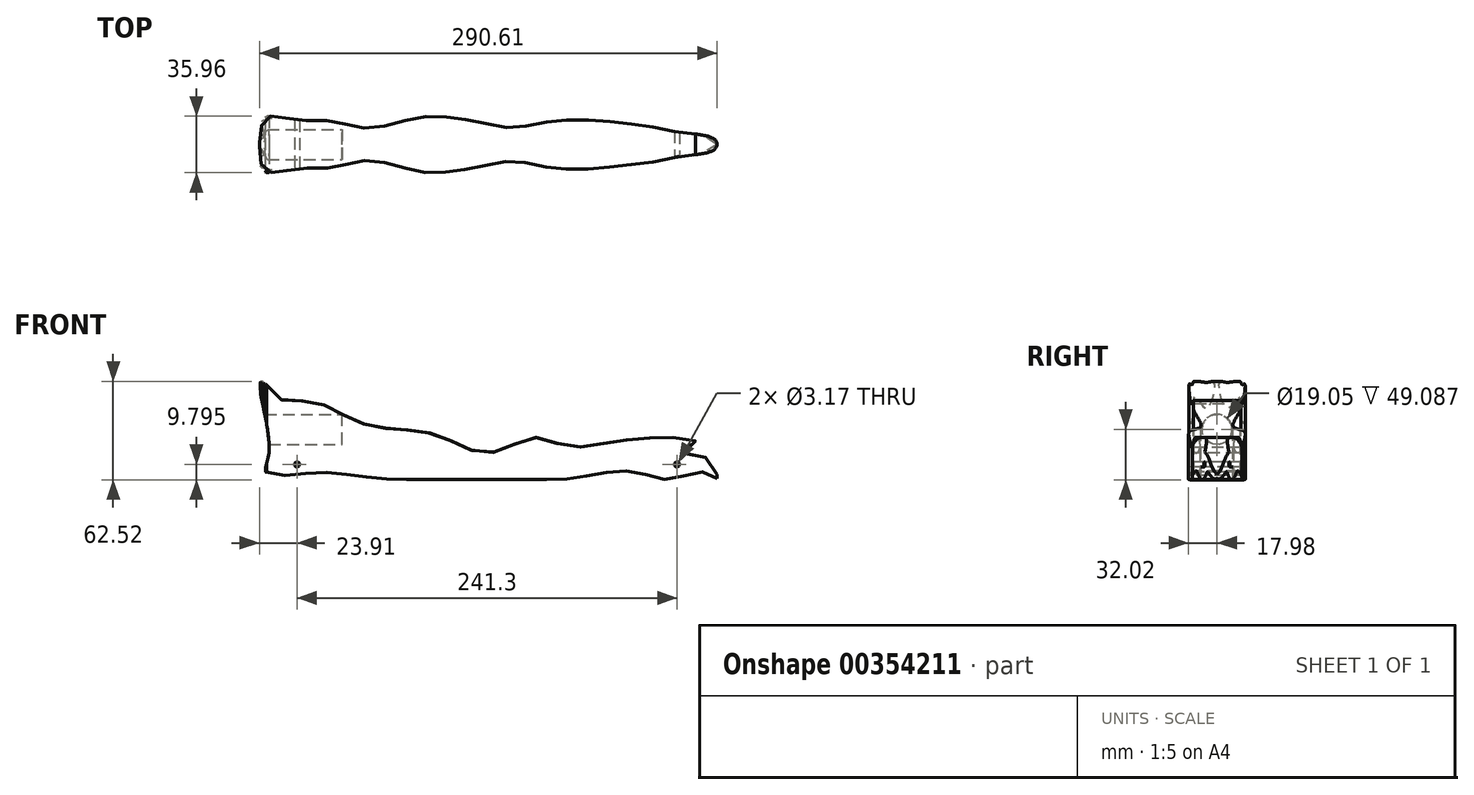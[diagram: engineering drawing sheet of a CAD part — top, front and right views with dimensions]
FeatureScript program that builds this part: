
annotation { "Feature Type Name" : "Feature", "Feature Type Description" : "" }
export const myFeature = defineFeature(function(context is Context, id is Id, definition is map)
    precondition{}
    {
        {
            var Q0;
            Q0=qCreatedBy(makeId("Front.planeOp"),FACE);
            var sketch = newSketch(context, id + "F0", { "sketchPlane" : qUnion([Q0])});
            skLineSegment(sketch, "E0.bottom", {"start": v(-146.05, 31.75) * mm, "end": v(146.05, 31.75) * mm, "construction": true});
            skLineSegment(sketch, "E0.top", {"start": v(-146.05, -31.75) * mm, "end": v(146.05, -31.75) * mm, "construction": true});
            skLineSegment(sketch, "E0.right", {"start": v(146.05, 31.75) * mm, "end": v(146.05, -31.75) * mm, "construction": true});
            skFitSpline(sketch, "E1", {"points": [v(-142.58, 16.26) * mm, v(-143.67, 30.49) * mm, v(-133.35, 21.5) * mm, v(-125.39, 16.19) * mm, v(-112.73, 18.18) * mm, v(-82.25, 5) * mm, v(-55.63, 0) * mm, v(-29, -4.68) * mm, v(0.8, -14.98) * mm, v(31.51, -5.09) * mm, v(49.97, -10.82) * mm, v(85.57, -7.1) * mm, v(132.37, -7.9) * mm, v(122.4, -14.23) * mm, v(138.05, -17.38) * mm, v(146.11, -29.06) * mm, v(145.87, -31.42) * mm, v(138.82, -27.27) * mm, v(115.42, -31.77) * mm, v(93.68, -26.94) * mm, v(68.53, -28.76) * mm, v(46.64, -31.75) * mm, v(19.14, -31.75) * mm, v(-6.95, -31.75) * mm, v(-28.05, -31.75) * mm, v(-58.89, -31.75) * mm, v(-90.08, -28.53) * mm, v(-109.1, -27.43) * mm, v(-139.94, -28.07) * mm, v(-138.86, -17.59) * mm, v(-142.58, 16.26) * mm]});
            skLineSegment(sketch, "E2.bottom", {"start": v(-146.05, 9.52) * mm, "end": v(-95.25, 9.52) * mm, "construction": true});
            skLineSegment(sketch, "E2.top", {"start": v(-141.83, -9.52) * mm, "end": v(-95.25, -9.52) * mm, "construction": true});
            skLineSegment(sketch, "E2.right", {"start": v(-95.25, 9.52) * mm, "end": v(-95.25, -9.52) * mm, "construction": true});
            skLineSegment(sketch, "E3", {"start": v(-146.05, 31.75) * mm, "end": v(-146.05, -31.75) * mm, "construction": true});
            skSolve(sketch);
        }
        {
            var Q0;
            Q0=qCreatedBy(makeId("Top.planeOp"),FACE);
            var sketch = newSketch(context, id + "F1", { "sketchPlane" : qUnion([Q0])});
            skLineSegment(sketch, "E4.bottom", {"start": v(-146.05, 22.22) * mm, "end": v(146.05, 22.23) * mm, "construction": true});
            skLineSegment(sketch, "E4.top", {"start": v(-146.05, -22.23) * mm, "end": v(146.05, -22.22) * mm, "construction": true});
            skLineSegment(sketch, "E4.left", {"start": v(-146.05, 22.22) * mm, "end": v(-146.05, -22.23) * mm, "construction": true});
            skLineSegment(sketch, "E4.right", {"start": v(146.05, 22.22) * mm, "end": v(146.05, -22.22) * mm, "construction": true});
            skLineSegment(sketch, "E5", {"start": v(-146.05, 0) * mm, "end": v(146.05, 0) * mm, "construction": true});
            skFitSpline(sketch, "E6", {"points": [v(-146.05, 0) * mm, v(-143.6, 14.28) * mm, v(-139.95, 15.87) * mm, v(-140.63, 17.47) * mm, v(-114.36, 14.96) * mm, v(-97, 14.73) * mm, v(-76.9, 10.16) * mm, v(-49.95, 15.65) * mm, v(-31.68, 17.93) * mm, v(-8.84, 14.96) * mm, v(0.99, 12.9) * mm, v(17.2, 10.62) * mm, v(34.8, 13.82) * mm, v(61.97, 15.65) * mm, v(86.64, 13.36) * mm, v(105.83, 11.08) * mm, v(117.7, 8.57) * mm, v(123.64, 7.42) * mm, v(132.55, 6.5) * mm, v(146.05, 0) * mm], "startDerivative": vector(484.77, 360.66) * mm, "endDerivative": vector(0, -277.49) * mm});
            skFitSpline(sketch, "E7.MirrorCS", {"points": [v(-146.05, 0) * mm, v(-143.6, -14.28) * mm, v(-139.95, -15.87) * mm, v(-140.63, -17.47) * mm, v(-114.36, -14.96) * mm, v(-97, -14.73) * mm, v(-76.9, -10.16) * mm, v(-49.95, -15.65) * mm, v(-31.68, -17.93) * mm, v(-8.84, -14.96) * mm, v(0.99, -12.9) * mm, v(17.2, -10.62) * mm, v(34.8, -13.82) * mm, v(61.97, -15.65) * mm, v(86.64, -13.36) * mm, v(105.83, -11.08) * mm, v(117.7, -8.57) * mm, v(123.64, -7.42) * mm, v(132.55, -6.5) * mm, v(146.05, 0) * mm], "startDerivative": vector(484.77, -360.66) * mm, "endDerivative": vector(0, 277.49) * mm});
            skLineSegment(sketch, "E8.MirrorCS", {"start": v(-146.05, -22.23) * mm, "end": v(146.05, -22.23) * mm});
            skSolve(sketch);
        }
        {
            var Q0;
            Q0=qCreatedBy(makeId("Right.planeOp"),FACE);
            var sketch = newSketch(context, id + "F2", { "sketchPlane" : qUnion([Q0])});
            skCircle(sketch, "E9", {"center": v(0, 0) * mm, "radius": 9.53 * mm});
            skSolve(sketch);
        }
        {
            var Q0;
            Q0=qCreatedBy(makeId("Front.planeOp"),FACE);
            var sketch = newSketch(context, id + "F3", { "sketchPlane" : qUnion([Q0])});
            skCircle(sketch, "E10", {"center": v(-120.65, -22.22) * mm, "radius": 1.59 * mm});
            skCircle(sketch, "E11", {"center": v(120.65, -22.23) * mm, "radius": 1.59 * mm});
            skSolve(sketch);
        }
        {
            var Q0;
            Q0=qSketchRegion(id+"F0",true);
            extrude(context, id + "F4", {"entities" : qUnion([Q0]), "depth" : 44.45 * mm, "symmetric" : true});
        }
        {
            var Q0;
            Q0=qSketchRegion(id+"F1",true);
            extrude(context, id + "F5", {"entities" : qUnion([Q0]), "operationType" : NewBodyOperationType.INTERSECT, "endBound" : BoundingType.THROUGH_ALL, "oppositeDirection" : true, "depth" : 60.96 * mm, "hasSecondDirection" : true, "secondDirectionBound" : BoundingType.THROUGH_ALL, "secondDirectionOppositeDirection" : false, "secondDirectionDepth" : 25.4 * mm});
        }
        {
            var Q0;
            Q0=qSketchRegion(id+"F2",true);
            extrude(context, id + "F6", {"entities" : qUnion([Q0]), "operationType" : NewBodyOperationType.REMOVE, "oppositeDirection" : true, "depth" : 152.4 * mm, "hasSecondDirection" : true, "secondDirectionOppositeDirection" : true, "secondDirectionDepth" : 92.07 * mm});
        }
        {
            var Q0;
            Q0=qSketchRegion(id+"F3",true);
            extrude(context, id + "F7", {"entities" : qUnion([Q0]), "operationType" : NewBodyOperationType.REMOVE, "oppositeDirection" : true, "depth" : 50.8 * mm, "symmetric" : true});
        }
    });
